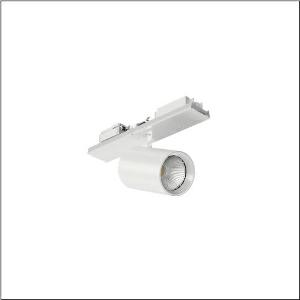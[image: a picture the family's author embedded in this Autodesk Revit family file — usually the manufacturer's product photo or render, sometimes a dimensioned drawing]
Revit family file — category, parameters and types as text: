
# Revit family: licross_r__spot_31_51sl13da43b_6d5a
name_source: partatom
category: Lighting Fixtures
units: mm (PartAtom-declared; Revit-internal decimal feet)

## family parameters
Cut with Voids When Loaded = No
Host = Face
Light Source = No
Part Type = Normal
Room Calculation Point = No
Round Connector Dimension = Use Diameter
Shared = No

## types (1)
- --- (1 x LED, 3680 lm, 28.6 W, 4000K)
    Apparent Load = 29 VA
    CIE Flux Codes = 92 97 99 100 100
    Color Rendering = 90
    Color Temperature = 4000K
    Default Elevation = 1800 mm
    Description = Licross® Spot 31, directional spotlight, light control with lens, of plastic, LED rated luminous flux: 3.680lm, light colour: 940, with plug, 5-pole, mains connection: 220..240V, AC, 50/60Hz, of aluminium, traffic white (RAL 9016), length: 140mm, diameter: 90mm, protection rating (complete): IP20, insulation class (complete): insulation class I (protective earthing), certification: CE, packaging unit: 1 piece
    Height = 175 mm
    Lamp = 1 x LED
    Lamp Light Flux = 3680 lm
    Lamp Power = 28.6 W
    Lamp count = 1
    Length = 90 mm
    Luminous efficacy = 129 lm/W
    Manufacturer = Siteco
    ModVariant = No
    Model = 51SL13DA43B
    Mounting Place = Ceiling
    Mounting Type = Pendant
    Number of Poles = 1
    OnlyDefault = Yes
    Power Factor = 1
    Product Name = Licross® Spot 31
    Product group = directional spotlight
    ProductGroupID = 905
    Protection Class = Protection class I
    Protection Degree = IP 20
    RLX_Detail_Level = 1
    RLX_Emergency_Light_Flux = 0 lm
    RLX_Emergency_Type = 0
    RLX_Emergency_Type_DB = No
    RlxData = <blob elided: 14813 chars, md5=0ea09f2f>
    Socket = socket
    Standby Power = 0 W
    System Light Flux = 3680 lm
    System Power = 29 W
    Type Comments = factory setting: luminous flux: 100 % | (ON | ON | ON) | 700 mA
    Type Image = l_1245720.jpg
    URL = http://relux.com
    VarID = @adj_081875
    Voltage = 0 V
    Weight = 0.00 kg
    Width = 0 mm  [stored 0 ft]

note: [stored X ft] marks values corroborated as IEEE doubles in the binary element streams (Revit-internal decimal feet)

## geometry (parser evidence)
native form markers: Sweep x11
no freeform markers — native parametric forms only
